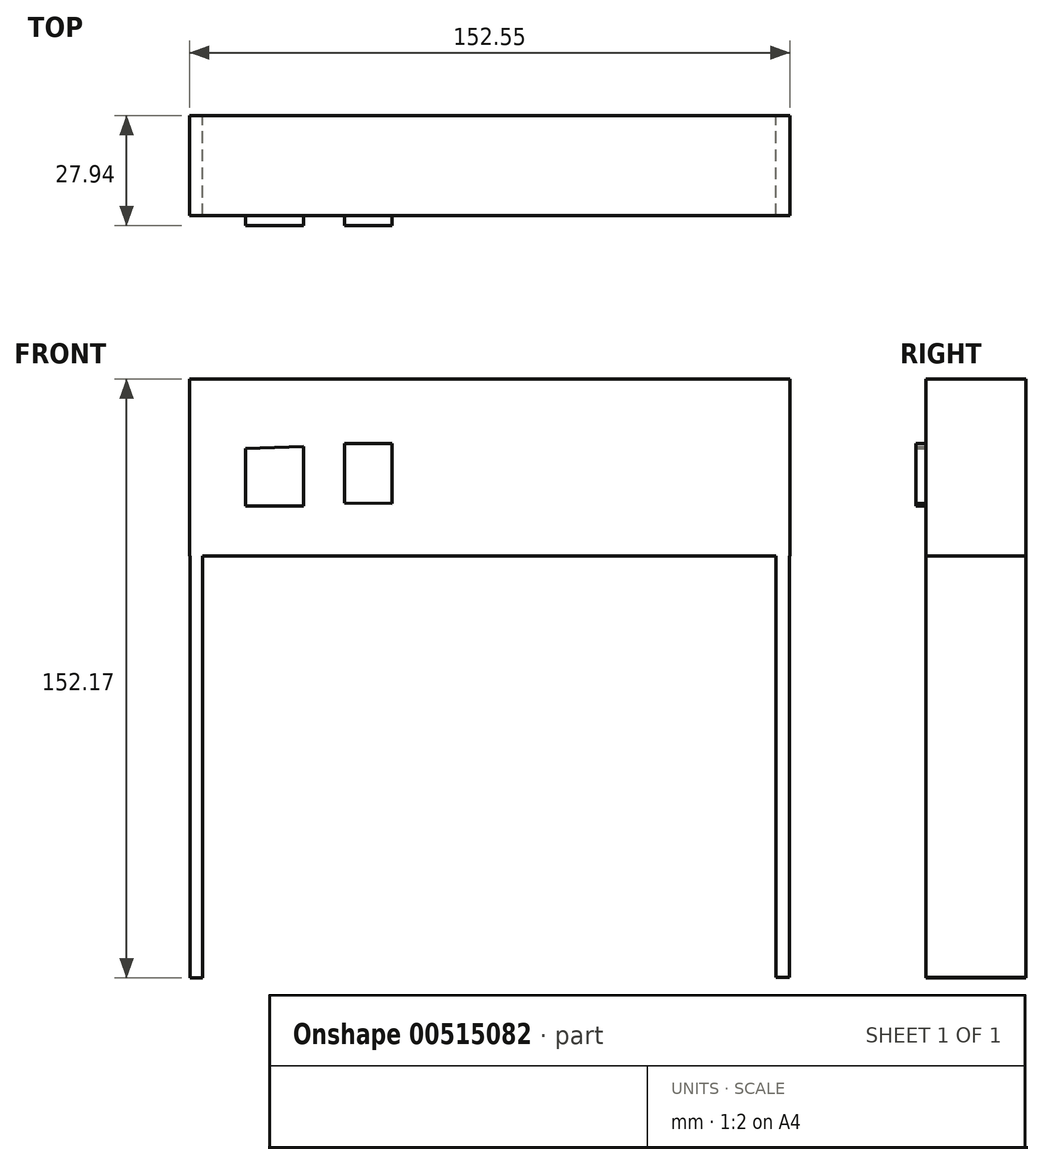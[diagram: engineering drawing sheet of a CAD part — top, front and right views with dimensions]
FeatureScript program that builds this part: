
annotation { "Feature Type Name" : "Feature", "Feature Type Description" : "" }
export const myFeature = defineFeature(function(context is Context, id is Id, definition is map)
    precondition{}
    {
        {
            var Q0;
            Q0=qCreatedBy(makeId("Front.planeOp"),FACE);
            var sketch = newSketch(context, id + "F0", { "sketchPlane" : qUnion([Q0])});
            skLineSegment(sketch, "E0.bottom", {"start": v(-76.23, 76.23) * mm, "end": v(76.32, 76.23) * mm});
            skLineSegment(sketch, "E0.top", {"start": v(-76.23, 31.27) * mm, "end": v(76.32, 31.27) * mm});
            skLineSegment(sketch, "E0.left", {"start": v(-76.23, 76.23) * mm, "end": v(-76.23, 31.27) * mm});
            skLineSegment(sketch, "E0.right", {"start": v(76.32, 76.23) * mm, "end": v(76.32, 31.27) * mm});
            skLineSegment(sketch, "E1.bottom", {"start": v(-76.07, -75.94) * mm, "end": v(-72.86, -75.94) * mm});
            skLineSegment(sketch, "E1.top", {"start": v(-76.07, 76.23) * mm, "end": v(-72.86, 76.23) * mm});
            skLineSegment(sketch, "E1.left", {"start": v(-76.07, -75.94) * mm, "end": v(-76.07, 76.23) * mm});
            skLineSegment(sketch, "E1.right", {"start": v(-72.86, -75.94) * mm, "end": v(-72.86, 76.23) * mm});
            skLineSegment(sketch, "E2.bottom", {"start": v(76.14, -75.84) * mm, "end": v(72.73, -75.84) * mm});
            skLineSegment(sketch, "E2.top", {"start": v(76.14, 76.23) * mm, "end": v(72.73, 76.23) * mm});
            skLineSegment(sketch, "E2.left", {"start": v(76.14, -75.84) * mm, "end": v(76.14, 76.23) * mm});
            skLineSegment(sketch, "E2.right", {"start": v(72.73, -75.84) * mm, "end": v(72.73, 76.23) * mm});
            skSolve(sketch);
        }
        {
            var Q0;
            Q0 = qSketchRegion(id + "F0", true);
            extrude(context, id + "F1", {"entities" : qUnion([Q0]), "depth" : 25.4 * mm, "offsetDistance" : 25.4 * mm});
        }
        {
            var Q0;
            Q0=makeQuery(id+"F1.opExtrude","CAP_FACE",FACE,{"disambiguationData":[OSD([sQuery(id+"F0.wireOp",EDGE,"E0.bottom"),sQuery(id+"F0.wireOp",EDGE,"E0.top"),sQuery(id+"F0.wireOp",EDGE,"E0.left"),sQuery(id+"F0.wireOp",EDGE,"E0.right"),sQuery(id+"F0.wireOp",EDGE,"E1.bottom"),sQuery(id+"F0.wireOp",EDGE,"E1.top"),sQuery(id+"F0.wireOp",EDGE,"E1.left"),sQuery(id+"F0.wireOp",EDGE,"E1.right"),sQuery(id+"F0.wireOp",EDGE,"E2.bottom"),sQuery(id+"F0.wireOp",EDGE,"E2.top"),sQuery(id+"F0.wireOp",EDGE,"E2.left"),sQuery(id+"F0.wireOp",EDGE,"E2.right")])],"isStart":false});
            var sketch = newSketch(context, id + "F2", { "sketchPlane" : qUnion([Q0])});
            skLineSegment(sketch, "E3", {"start": v(-62, 58.63) * mm, "end": v(-62, 43.98) * mm});
            skLineSegment(sketch, "E4", {"start": v(-62, 43.98) * mm, "end": v(-47.26, 43.98) * mm});
            skLineSegment(sketch, "E5", {"start": v(-47.26, 43.98) * mm, "end": v(-47.26, 59.05) * mm});
            skLineSegment(sketch, "E6", {"start": v(-47.26, 59.05) * mm, "end": v(-62, 58.63) * mm});
            skLineSegment(sketch, "E7", {"start": v(-36.83, 44.8) * mm, "end": v(-36.83, 59.83) * mm});
            skLineSegment(sketch, "E8", {"start": v(-36.83, 59.83) * mm, "end": v(-24.8, 59.83) * mm});
            skLineSegment(sketch, "E9", {"start": v(-24.8, 59.83) * mm, "end": v(-24.8, 44.65) * mm});
            skLineSegment(sketch, "E10", {"start": v(-36.83, 44.8) * mm, "end": v(-24.8, 44.65) * mm});
            skSolve(sketch);
        }
        {
            var Q0;
            Q0=makeQuery(id+"F2.imprint","IMPRINT",FACE,{"disambiguationData":[TD([[makeQuery(id+"F2.imprint","IMPRINT",EDGE,{"derivedFrom":sQuery(id+"F2.wireOp",EDGE,"E7")}),-1.0]])]});
            var Q1;
            Q1=makeQuery(id+"F2.imprint","IMPRINT",FACE,{"disambiguationData":[TD([[makeQuery(id+"F2.imprint","IMPRINT",EDGE,{"derivedFrom":sQuery(id+"F2.wireOp",EDGE,"E3")}),1.0]])]});
            var Q2;
            Q2=sQuery(id+"F2.wireOp",EDGE,"E7");
            var Q3;
            Q3=sQuery(id+"F2.wireOp",EDGE,"E6");
            var Q4;
            Q4=sQuery(id+"F2.wireOp",EDGE,"E3");
            var Q5;
            Q5=sQuery(id+"F2.wireOp",EDGE,"E9");
            var Q6;
            Q6=sQuery(id+"F2.wireOp",EDGE,"E5");
            var Q7;
            Q7=sQuery(id+"F2.wireOp",EDGE,"E8");
            var Q8;
            Q8=sQuery(id+"F2.wireOp",EDGE,"E10");
            var Q9;
            Q9=sQuery(id+"F2.wireOp",EDGE,"E4");
            extrude(context, id + "F3", {"entities" : qUnion([Q0, Q1]), "operationType" : NewBodyOperationType.ADD, "surfaceEntities" : qUnion([Q2, Q3, Q4, Q5, Q6, Q7, Q8, Q9]), "depth" : 2.54 * mm, "offsetDistance" : 25.4 * mm});
        }
    });
